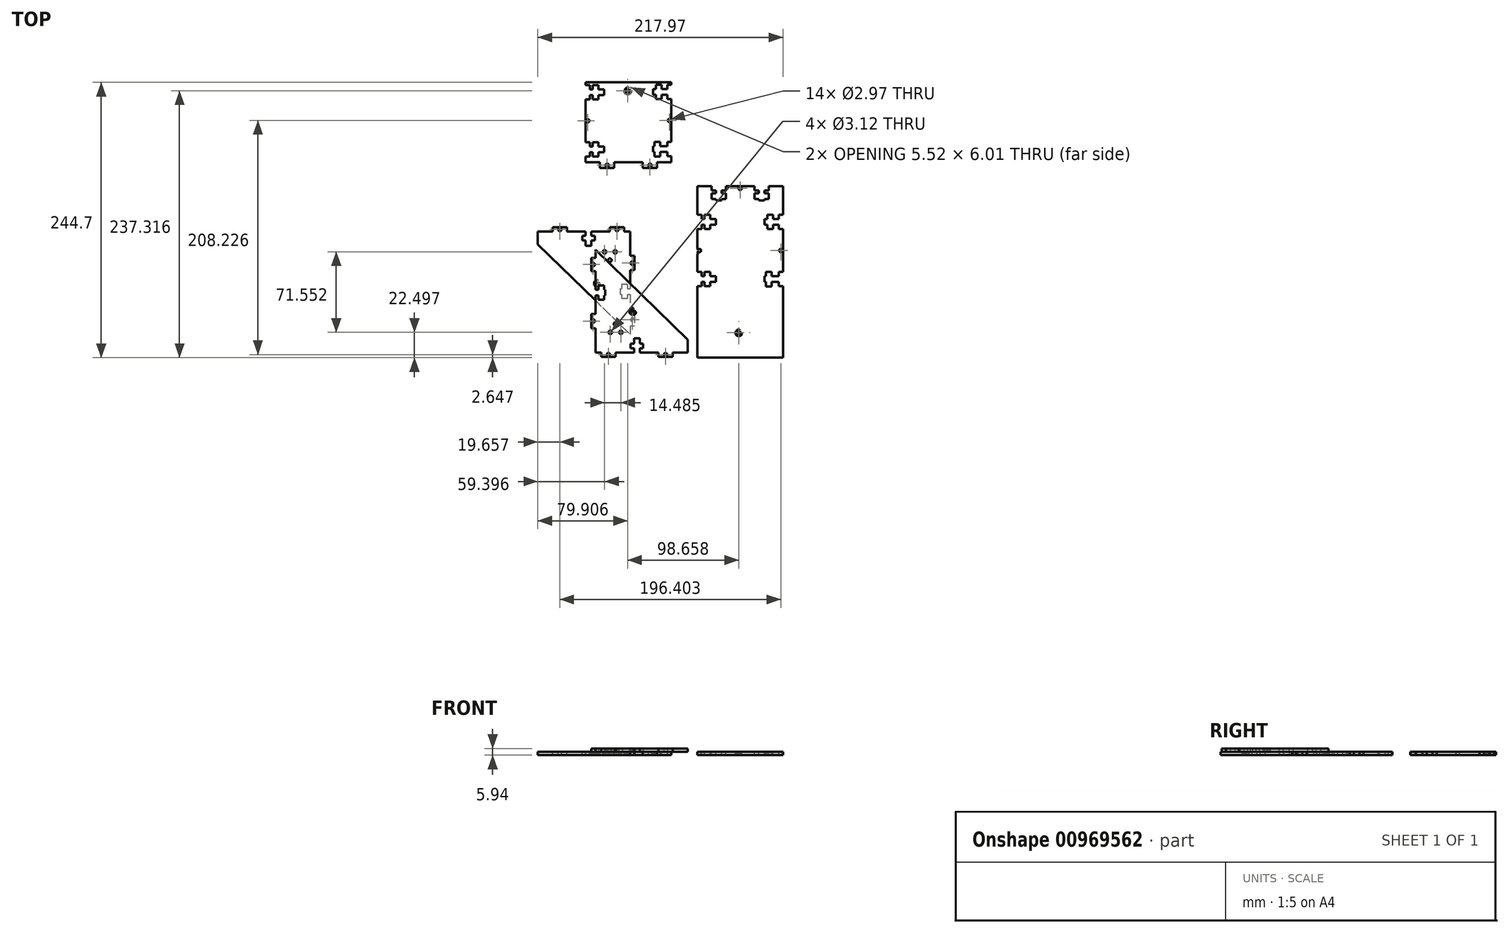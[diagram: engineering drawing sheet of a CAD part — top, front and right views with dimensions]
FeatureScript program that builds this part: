
annotation { "Feature Type Name" : "Feature", "Feature Type Description" : "" }
export const myFeature = defineFeature(function(context is Context, id is Id, definition is map)
    precondition{}
    {
        {
            var Q0;
            Q0=qCreatedBy(makeId("Top.planeOp"),FACE);
            var sketch = newSketch(context, id + "F0", { "sketchPlane" : qUnion([Q0])});
            skLineSegment(sketch, "E0.bottom", {"start": v(-31.04, 87.19) * mm, "end": v(45.16, 87.19) * mm});
            skLineSegment(sketch, "E0.top", {"start": v(-31.04, -65.21) * mm, "end": v(45.16, -65.21) * mm});
            skLineSegment(sketch, "E0.left", {"start": v(-31.04, 87.19) * mm, "end": v(-31.04, -65.21) * mm});
            skLineSegment(sketch, "E0.right", {"start": v(45.16, 87.19) * mm, "end": v(45.16, -65.21) * mm});
            skSolve(sketch);
        }
        {
            var Q0;
            Q0 = qSketchRegion(id + "F0", true);
            extrude(context, id + "F1", {"entities" : qUnion([Q0]), "depth" : 2.97 * mm, "offsetDistance" : 25.4 * mm});
        }
        {
            var Q0;
            Q0=makeQuery(id+"F1.opExtrude","CAP_FACE",FACE,{"disambiguationData":[OSD([sQuery(id+"F0.wireOp",EDGE,"E0.bottom"),sQuery(id+"F0.wireOp",EDGE,"E0.top"),sQuery(id+"F0.wireOp",EDGE,"E0.left"),sQuery(id+"F0.wireOp",EDGE,"E0.right")])],"isStart":false});
            var sketch = newSketch(context, id + "F2", { "sketchPlane" : qUnion([Q0])});
            skLineSegment(sketch, "E1.bottom", {"start": v(-31.04, 61.79) * mm, "end": v(-27.23, 61.79) * mm});
            skLineSegment(sketch, "E1.top", {"start": v(-31.04, 49.09) * mm, "end": v(-27.23, 49.09) * mm});
            skLineSegment(sketch, "E1.left", {"start": v(-31.04, 61.79) * mm, "end": v(-31.04, 49.09) * mm});
            skLineSegment(sketch, "E1.right", {"start": v(-27.23, 61.79) * mm, "end": v(-27.23, 49.09) * mm});
            skLineSegment(sketch, "E2", {"start": v(-24.7, 61.79) * mm, "end": v(-24.7, 87.19) * mm, "construction": true});
            skLineSegment(sketch, "E3", {"start": v(-31.04, 33.1) * mm, "end": v(-31.04, 33.1) * mm});
            skLineSegment(sketch, "E4.bottom", {"start": v(-14.53, 52.9) * mm, "end": v(-39.93, 52.9) * mm});
            skLineSegment(sketch, "E4.top", {"start": v(-14.53, 57.98) * mm, "end": v(-39.93, 57.98) * mm});
            skLineSegment(sketch, "E4.left", {"start": v(-14.53, 52.9) * mm, "end": v(-14.53, 57.98) * mm});
            skLineSegment(sketch, "E4.right", {"start": v(-39.93, 52.9) * mm, "end": v(-39.93, 57.98) * mm});
            skPoint(sketch, "E4.middle", {"position": v(-27.23, 55.44) * mm});
            skLineSegment(sketch, "E5.bottom", {"start": v(-24.7, 61.79) * mm, "end": v(-19.61, 61.79) * mm});
            skLineSegment(sketch, "E5.top", {"start": v(-24.7, 49.09) * mm, "end": v(-19.61, 49.09) * mm});
            skLineSegment(sketch, "E5.left", {"start": v(-24.7, 61.79) * mm, "end": v(-24.7, 49.09) * mm});
            skLineSegment(sketch, "E5.right", {"start": v(-19.61, 61.79) * mm, "end": v(-19.61, 49.09) * mm});
            skLineSegment(sketch, "E6.bottom", {"start": v(-31.04, 10.99) * mm, "end": v(-27.23, 10.99) * mm});
            skLineSegment(sketch, "E6.top", {"start": v(-31.04, -1.71) * mm, "end": v(-27.23, -1.71) * mm});
            skLineSegment(sketch, "E6.left", {"start": v(-31.04, 10.99) * mm, "end": v(-31.04, -1.71) * mm});
            skLineSegment(sketch, "E6.right", {"start": v(-27.23, 10.99) * mm, "end": v(-27.23, -1.71) * mm});
            skLineSegment(sketch, "E7", {"start": v(11.23, 8.06) * mm, "end": v(11.23, 8.06) * mm});
            skLineSegment(sketch, "E8.bottom", {"start": v(-14.53, 2.1) * mm, "end": v(-39.93, 2.1) * mm});
            skLineSegment(sketch, "E8.top", {"start": v(-14.53, 7.18) * mm, "end": v(-39.93, 7.18) * mm});
            skLineSegment(sketch, "E8.left", {"start": v(-14.53, 2.1) * mm, "end": v(-14.53, 7.18) * mm});
            skLineSegment(sketch, "E8.right", {"start": v(-39.93, 2.1) * mm, "end": v(-39.93, 7.18) * mm});
            skPoint(sketch, "E8.middle", {"position": v(-27.23, 4.64) * mm});
            skLineSegment(sketch, "E9.bottom", {"start": v(-24.7, 10.99) * mm, "end": v(-19.61, 10.99) * mm});
            skLineSegment(sketch, "E9.top", {"start": v(-24.7, -1.71) * mm, "end": v(-19.61, -1.71) * mm});
            skLineSegment(sketch, "E9.left", {"start": v(-24.7, 10.99) * mm, "end": v(-24.7, -1.71) * mm});
            skLineSegment(sketch, "E9.right", {"start": v(-19.61, 10.99) * mm, "end": v(-19.61, -1.71) * mm});
            skLineSegment(sketch, "E10.bottom", {"start": v(-18.34, 87.19) * mm, "end": v(-5.64, 87.19) * mm});
            skLineSegment(sketch, "E10.top", {"start": v(-18.34, 83.38) * mm, "end": v(-5.64, 83.38) * mm});
            skLineSegment(sketch, "E10.left", {"start": v(-18.34, 87.19) * mm, "end": v(-18.34, 83.38) * mm});
            skLineSegment(sketch, "E10.right", {"start": v(-5.64, 87.19) * mm, "end": v(-5.64, 83.38) * mm});
            skLineSegment(sketch, "E11.bottom", {"start": v(19.76, 87.19) * mm, "end": v(32.46, 87.19) * mm});
            skLineSegment(sketch, "E11.top", {"start": v(19.76, 83.38) * mm, "end": v(32.46, 83.38) * mm});
            skLineSegment(sketch, "E11.left", {"start": v(19.76, 87.19) * mm, "end": v(19.76, 83.38) * mm});
            skLineSegment(sketch, "E11.right", {"start": v(32.46, 87.19) * mm, "end": v(32.46, 83.38) * mm});
            skLineSegment(sketch, "E12", {"start": v(-18.34, 85.28) * mm, "end": v(-31.04, 85.28) * mm, "construction": true});
            skLineSegment(sketch, "E13", {"start": v(32.46, 85.28) * mm, "end": v(45.16, 85.28) * mm, "construction": true});
            skLineSegment(sketch, "E14.bottom", {"start": v(-9.45, 74.49) * mm, "end": v(-14.53, 74.49) * mm});
            skLineSegment(sketch, "E14.top", {"start": v(-9.45, 99.89) * mm, "end": v(-14.53, 99.89) * mm});
            skLineSegment(sketch, "E14.left", {"start": v(-9.45, 74.49) * mm, "end": v(-9.45, 99.89) * mm});
            skLineSegment(sketch, "E14.right", {"start": v(-14.53, 74.49) * mm, "end": v(-14.53, 99.89) * mm});
            skPoint(sketch, "E14.middle", {"position": v(-12, 87.19) * mm});
            skLineSegment(sketch, "E15.bottom", {"start": v(-5.64, 80.84) * mm, "end": v(-18.34, 80.84) * mm});
            skLineSegment(sketch, "E15.top", {"start": v(-5.64, 75.76) * mm, "end": v(-18.34, 75.76) * mm});
            skLineSegment(sketch, "E15.left", {"start": v(-5.64, 80.84) * mm, "end": v(-5.64, 75.76) * mm});
            skLineSegment(sketch, "E15.right", {"start": v(-18.34, 80.84) * mm, "end": v(-18.34, 75.76) * mm});
            skLineSegment(sketch, "E16", {"start": v(-5.64, 80.84) * mm, "end": v(-5.64, 83.38) * mm, "construction": true});
            skLineSegment(sketch, "E17.bottom", {"start": v(28.65, 74.49) * mm, "end": v(23.57, 74.49) * mm});
            skLineSegment(sketch, "E17.top", {"start": v(28.65, 99.89) * mm, "end": v(23.57, 99.89) * mm});
            skLineSegment(sketch, "E17.left", {"start": v(28.65, 74.49) * mm, "end": v(28.65, 99.89) * mm});
            skLineSegment(sketch, "E17.right", {"start": v(23.57, 74.49) * mm, "end": v(23.57, 99.89) * mm});
            skPoint(sketch, "E17.middle", {"position": v(26.1, 87.19) * mm});
            skLineSegment(sketch, "E18.bottom", {"start": v(32.46, 80.84) * mm, "end": v(19.76, 80.84) * mm});
            skLineSegment(sketch, "E18.top", {"start": v(32.46, 75.76) * mm, "end": v(19.76, 75.76) * mm});
            skLineSegment(sketch, "E18.left", {"start": v(32.46, 80.84) * mm, "end": v(32.46, 75.76) * mm});
            skLineSegment(sketch, "E18.right", {"start": v(19.76, 80.84) * mm, "end": v(19.76, 75.76) * mm});
            skLineSegment(sketch, "E19", {"start": v(19.76, 80.84) * mm, "end": v(19.76, 83.38) * mm, "construction": true});
            skLineSegment(sketch, "E20", {"start": v(-29.14, 49.09) * mm, "end": v(-29.14, 10.99) * mm, "construction": true});
            skCircle(sketch, "E21", {"center": v(-29.14, 30.04) * mm, "radius": 1.49 * mm});
            skLineSegment(sketch, "E22", {"start": v(-5.64, 85.28) * mm, "end": v(19.76, 85.28) * mm, "construction": true});
            skCircle(sketch, "E23", {"center": v(7.06, 85.28) * mm, "radius": 1.49 * mm});
            skLineSegment(sketch, "E24", {"start": v(-27.23, 49.09) * mm, "end": v(-24.7, 49.09) * mm, "construction": true});
            skLineSegment(sketch, "E25.bottom", {"start": v(45.16, 61.79) * mm, "end": v(41.35, 61.79) * mm});
            skLineSegment(sketch, "E25.top", {"start": v(45.16, 49.09) * mm, "end": v(41.35, 49.09) * mm});
            skLineSegment(sketch, "E25.left", {"start": v(45.16, 61.79) * mm, "end": v(45.16, 49.09) * mm});
            skLineSegment(sketch, "E25.right", {"start": v(41.35, 61.79) * mm, "end": v(41.35, 49.09) * mm});
            skLineSegment(sketch, "E26", {"start": v(41.35, 61.79) * mm, "end": v(41.35, 87.19) * mm, "construction": true});
            skLineSegment(sketch, "E27.bottom", {"start": v(28.65, 57.98) * mm, "end": v(54.05, 57.98) * mm});
            skLineSegment(sketch, "E27.top", {"start": v(28.65, 52.9) * mm, "end": v(54.05, 52.9) * mm});
            skLineSegment(sketch, "E27.left", {"start": v(28.65, 57.98) * mm, "end": v(28.65, 52.9) * mm});
            skLineSegment(sketch, "E27.right", {"start": v(54.05, 57.98) * mm, "end": v(54.05, 52.9) * mm});
            skPoint(sketch, "E27.middle", {"position": v(41.35, 55.44) * mm});
            skLineSegment(sketch, "E28.bottom", {"start": v(36.27, 61.79) * mm, "end": v(31.19, 61.79) * mm});
            skLineSegment(sketch, "E28.top", {"start": v(36.27, 49.09) * mm, "end": v(31.19, 49.09) * mm});
            skLineSegment(sketch, "E28.left", {"start": v(36.27, 61.79) * mm, "end": v(36.27, 49.09) * mm});
            skLineSegment(sketch, "E28.right", {"start": v(31.19, 61.79) * mm, "end": v(31.19, 49.09) * mm});
            skLineSegment(sketch, "E29", {"start": v(36.27, 49.09) * mm, "end": v(41.35, 49.09) * mm, "construction": true});
            skLineSegment(sketch, "E30.bottom", {"start": v(45.16, 10.99) * mm, "end": v(41.35, 10.99) * mm});
            skLineSegment(sketch, "E30.top", {"start": v(45.16, -1.71) * mm, "end": v(41.35, -1.71) * mm});
            skLineSegment(sketch, "E30.left", {"start": v(45.16, 10.99) * mm, "end": v(45.16, -1.71) * mm});
            skLineSegment(sketch, "E30.right", {"start": v(41.35, 10.99) * mm, "end": v(41.35, -1.71) * mm});
            skLineSegment(sketch, "E31.bottom", {"start": v(28.65, 7.18) * mm, "end": v(54.05, 7.18) * mm});
            skLineSegment(sketch, "E31.top", {"start": v(28.65, 2.1) * mm, "end": v(54.05, 2.1) * mm});
            skLineSegment(sketch, "E31.left", {"start": v(28.65, 7.18) * mm, "end": v(28.65, 2.1) * mm});
            skLineSegment(sketch, "E31.right", {"start": v(54.05, 7.18) * mm, "end": v(54.05, 2.1) * mm});
            skPoint(sketch, "E31.middle", {"position": v(41.35, 4.64) * mm});
            skLineSegment(sketch, "E32.bottom", {"start": v(34.98, 10.99) * mm, "end": v(30.02, 10.99) * mm});
            skLineSegment(sketch, "E32.top", {"start": v(34.98, -2) * mm, "end": v(30.02, -2) * mm});
            skLineSegment(sketch, "E32.left", {"start": v(34.98, 10.99) * mm, "end": v(34.98, -2) * mm});
            skLineSegment(sketch, "E32.right", {"start": v(30.02, 10.99) * mm, "end": v(30.02, -2) * mm});
            skLineSegment(sketch, "E33", {"start": v(41.35, 49.09) * mm, "end": v(43.25, 49.09) * mm, "construction": true});
            skLineSegment(sketch, "E34", {"start": v(43.25, 10.99) * mm, "end": v(43.25, 49.09) * mm, "construction": true});
            skCircle(sketch, "E35", {"center": v(43.25, 30.04) * mm, "radius": 1.49 * mm});
            skSolve(sketch);
        }
        {
            var Q0;
            Q0 = qSketchRegion(id + "F2", true);
            extrude(context, id + "F3", {"entities" : qUnion([Q0]), "operationType" : NewBodyOperationType.REMOVE, "oppositeDirection" : true, "depth" : 25.4 * mm, "offsetDistance" : 25.4 * mm});
        }
        {
            var Q0;
            Q0=qCreatedBy(makeId("Top.planeOp"),FACE);
            var sketch = newSketch(context, id + "F4", { "sketchPlane" : qUnion([Q0])});
            skLineSegment(sketch, "E36.bottom", {"start": v(-43.25, 86.15) * mm, "end": v(-129.12, 86.15) * mm});
            skLineSegment(sketch, "E36.top", {"start": v(-43.25, -66.25) * mm, "end": v(-129.12, -66.25) * mm});
            skLineSegment(sketch, "E36.left", {"start": v(-43.25, 86.15) * mm, "end": v(-43.25, -66.25) * mm});
            skLineSegment(sketch, "E36.right", {"start": v(-129.12, 86.15) * mm, "end": v(-129.12, -66.25) * mm});
            skSolve(sketch);
        }
        {
            var Q0;
            Q0 = qSketchRegion(id + "F4", true);
            extrude(context, id + "F5", {"entities" : qUnion([Q0]), "depth" : 2.97 * mm, "offsetDistance" : 25.4 * mm});
        }
        {
            var Q0;
            Q0=makeQuery(id+"F5.opExtrude","CAP_FACE",FACE,{"disambiguationData":[OSD([sQuery(id+"F4.wireOp",EDGE,"E36.bottom"),sQuery(id+"F4.wireOp",EDGE,"E36.top"),sQuery(id+"F4.wireOp",EDGE,"E36.left"),sQuery(id+"F4.wireOp",EDGE,"E36.right")])],"isStart":false});
            var sketch = newSketch(context, id + "F6", { "sketchPlane" : qUnion([Q0])});
            skLineSegment(sketch, "E37.bottom", {"start": v(-43.25, 86.15) * mm, "end": v(-47.06, 86.15) * mm});
            skLineSegment(sketch, "E37.top", {"start": v(-43.25, 60.75) * mm, "end": v(-47.06, 60.75) * mm});
            skLineSegment(sketch, "E37.left", {"start": v(-43.25, 86.15) * mm, "end": v(-43.25, 60.75) * mm});
            skLineSegment(sketch, "E37.right", {"start": v(-47.06, 86.15) * mm, "end": v(-47.06, 60.75) * mm});
            skLineSegment(sketch, "E38", {"start": v(-46.12, 86.15) * mm, "end": v(-46.12, 86.15) * mm});
            skLineSegment(sketch, "E39", {"start": v(-43.25, 68.93) * mm, "end": v(-43.25, 68.93) * mm});
            skLineSegment(sketch, "E40.bottom", {"start": v(-43.25, 48.05) * mm, "end": v(-47.06, 48.05) * mm});
            skLineSegment(sketch, "E40.top", {"start": v(-43.25, 9.95) * mm, "end": v(-47.06, 9.95) * mm});
            skLineSegment(sketch, "E40.left", {"start": v(-43.25, 48.05) * mm, "end": v(-43.25, 9.95) * mm});
            skLineSegment(sketch, "E40.right", {"start": v(-47.06, 48.05) * mm, "end": v(-47.06, 9.95) * mm});
            skLineSegment(sketch, "E41", {"start": v(-45.15, 60.75) * mm, "end": v(-45.15, 48.05) * mm, "construction": true});
            skLineSegment(sketch, "E42.bottom", {"start": v(-43.25, -1.8) * mm, "end": v(-47.06, -1.8) * mm});
            skLineSegment(sketch, "E42.top", {"start": v(-43.25, -174.53) * mm, "end": v(-47.06, -174.53) * mm});
            skLineSegment(sketch, "E42.left", {"start": v(-43.25, -1.8) * mm, "end": v(-43.25, -174.53) * mm});
            skLineSegment(sketch, "E42.right", {"start": v(-47.06, -1.8) * mm, "end": v(-47.06, -174.53) * mm});
            skLineSegment(sketch, "E43.bottom", {"start": v(-43.25, 35.35) * mm, "end": v(-47.06, 35.35) * mm});
            skLineSegment(sketch, "E43.top", {"start": v(-43.25, 22.65) * mm, "end": v(-47.06, 22.65) * mm});
            skLineSegment(sketch, "E43.left", {"start": v(-43.25, 35.35) * mm, "end": v(-43.25, 22.65) * mm});
            skLineSegment(sketch, "E43.right", {"start": v(-47.06, 35.35) * mm, "end": v(-47.06, 22.65) * mm});
            skLineSegment(sketch, "E44", {"start": v(-45.15, 48.05) * mm, "end": v(-45.15, 35.35) * mm, "construction": true});
            skLineSegment(sketch, "E45", {"start": v(-45.15, 9.95) * mm, "end": v(-45.15, 22.65) * mm, "construction": true});
            skLineSegment(sketch, "E46.bottom", {"start": v(-55.95, 31.54) * mm, "end": v(-30.55, 31.54) * mm});
            skLineSegment(sketch, "E46.top", {"start": v(-55.95, 26.46) * mm, "end": v(-30.55, 26.46) * mm});
            skLineSegment(sketch, "E46.left", {"start": v(-55.95, 31.54) * mm, "end": v(-55.95, 26.46) * mm});
            skLineSegment(sketch, "E46.right", {"start": v(-30.55, 31.54) * mm, "end": v(-30.55, 26.46) * mm});
            skPoint(sketch, "E46.middle", {"position": v(-43.25, 29) * mm});
            skLineSegment(sketch, "E47.bottom", {"start": v(-49.6, 35.35) * mm, "end": v(-54.68, 35.35) * mm});
            skLineSegment(sketch, "E47.top", {"start": v(-49.6, 22.65) * mm, "end": v(-54.68, 22.65) * mm});
            skLineSegment(sketch, "E47.left", {"start": v(-49.6, 35.35) * mm, "end": v(-49.6, 22.65) * mm});
            skLineSegment(sketch, "E47.right", {"start": v(-54.68, 35.35) * mm, "end": v(-54.68, 22.65) * mm});
            skLineSegment(sketch, "E48", {"start": v(-49.6, 33.67) * mm, "end": v(-47.06, 33.67) * mm, "construction": true});
            skCircle(sketch, "E49", {"center": v(-45.15, 54.4) * mm, "radius": 1.49 * mm});
            skLineSegment(sketch, "E50", {"start": v(-45.15, 9.95) * mm, "end": v(-45.15, -1.8) * mm, "construction": true});
            skCircle(sketch, "E51", {"center": v(-45.15, 4.08) * mm, "radius": 1.49 * mm});
            skLineSegment(sketch, "E52.bottom", {"start": v(-47.06, 82.34) * mm, "end": v(-52.31, 82.34) * mm});
            skLineSegment(sketch, "E52.top", {"start": v(-47.06, 86.15) * mm, "end": v(-52.31, 86.15) * mm});
            skLineSegment(sketch, "E52.left", {"start": v(-47.06, 82.34) * mm, "end": v(-47.06, 86.15) * mm});
            skLineSegment(sketch, "E52.right", {"start": v(-52.31, 82.34) * mm, "end": v(-52.31, 86.15) * mm});
            skLineSegment(sketch, "E53", {"start": v(-52.31, 82.34) * mm, "end": v(-65.01, 82.34) * mm, "construction": true});
            skLineSegment(sketch, "E54.bottom", {"start": v(-65.01, 82.34) * mm, "end": v(-103.11, 82.34) * mm});
            skLineSegment(sketch, "E54.top", {"start": v(-65.01, 86.15) * mm, "end": v(-103.11, 86.15) * mm});
            skLineSegment(sketch, "E54.left", {"start": v(-65.01, 82.34) * mm, "end": v(-65.01, 86.15) * mm});
            skLineSegment(sketch, "E54.right", {"start": v(-103.11, 82.34) * mm, "end": v(-103.11, 86.15) * mm});
            skLineSegment(sketch, "E55", {"start": v(-103.11, 82.34) * mm, "end": v(-115.81, 82.34) * mm, "construction": true});
            skLineSegment(sketch, "E56.bottom", {"start": v(-115.81, 82.34) * mm, "end": v(-130.63, 82.34) * mm});
            skLineSegment(sketch, "E56.top", {"start": v(-115.81, 87.7) * mm, "end": v(-130.63, 87.7) * mm});
            skLineSegment(sketch, "E56.left", {"start": v(-115.81, 82.34) * mm, "end": v(-115.81, 87.7) * mm});
            skLineSegment(sketch, "E56.right", {"start": v(-130.63, 82.34) * mm, "end": v(-130.63, 87.7) * mm});
            skLineSegment(sketch, "E57", {"start": v(-103.11, 84.25) * mm, "end": v(-115.81, 84.25) * mm, "construction": true});
            skCircle(sketch, "E58", {"center": v(-109.46, 84.25) * mm, "radius": 1.49 * mm});
            skLineSegment(sketch, "E59", {"start": v(-65.01, 84.25) * mm, "end": v(-52.31, 84.25) * mm, "construction": true});
            skCircle(sketch, "E60", {"center": v(-58.66, 84.25) * mm, "radius": 1.49 * mm});
            skLineSegment(sketch, "E61.bottom", {"start": v(-86.6, 69.64) * mm, "end": v(-81.52, 69.64) * mm});
            skLineSegment(sketch, "E61.top", {"start": v(-86.6, 95.04) * mm, "end": v(-81.52, 95.04) * mm});
            skLineSegment(sketch, "E61.left", {"start": v(-86.6, 69.64) * mm, "end": v(-86.6, 95.04) * mm});
            skLineSegment(sketch, "E61.right", {"start": v(-81.52, 69.64) * mm, "end": v(-81.52, 95.04) * mm});
            skPoint(sketch, "E61.middle", {"position": v(-84.06, 82.34) * mm});
            skLineSegment(sketch, "E62.bottom", {"start": v(-89.43, 78.63) * mm, "end": v(-78.4, 78.63) * mm});
            skLineSegment(sketch, "E62.top", {"start": v(-89.43, 74.47) * mm, "end": v(-78.4, 74.47) * mm});
            skLineSegment(sketch, "E62.left", {"start": v(-89.43, 78.63) * mm, "end": v(-89.43, 74.47) * mm});
            skLineSegment(sketch, "E62.right", {"start": v(-78.4, 78.63) * mm, "end": v(-78.4, 74.47) * mm});
            skSolve(sketch);
        }
        {
            var Q0;
            Q0 = qSketchRegion(id + "F6", true);
            extrude(context, id + "F7", {"entities" : qUnion([Q0]), "operationType" : NewBodyOperationType.REMOVE, "oppositeDirection" : true, "depth" : 25.4 * mm, "offsetDistance" : 25.4 * mm});
        }
        {
            var Q0;
            Q0=qCreatedBy(makeId("Top.planeOp"),FACE);
            var sketch = newSketch(context, id + "F8", { "sketchPlane" : qUnion([Q0])});
            skLineSegment(sketch, "E63.bottom", {"start": v(-30.12, 88.56) * mm, "end": v(46.08, 88.56) * mm});
            skLineSegment(sketch, "E63.top", {"start": v(-30.12, 164.76) * mm, "end": v(46.08, 164.76) * mm});
            skLineSegment(sketch, "E63.left", {"start": v(-30.12, 88.56) * mm, "end": v(-30.12, 164.76) * mm});
            skLineSegment(sketch, "E63.right", {"start": v(46.08, 88.56) * mm, "end": v(46.08, 164.76) * mm});
            skSolve(sketch);
        }
        {
            var Q0;
            Q0 = qSketchRegion(id + "F8", true);
            extrude(context, id + "F9", {"entities" : qUnion([Q0]), "depth" : 2.97 * mm, "offsetDistance" : 25.4 * mm});
        }
        {
            var Q0;
            Q0=makeQuery(id+"F9.opExtrude","CAP_FACE",FACE,{"disambiguationData":[OSD([sQuery(id+"F8.wireOp",EDGE,"E63.bottom"),sQuery(id+"F8.wireOp",EDGE,"E63.top"),sQuery(id+"F8.wireOp",EDGE,"E63.left"),sQuery(id+"F8.wireOp",EDGE,"E63.right")])],"isStart":false});
            var sketch = newSketch(context, id + "F10", { "sketchPlane" : qUnion([Q0])});
            skLineSegment(sketch, "E64.bottom", {"start": v(-30.12, 93.64) * mm, "end": v(-17.42, 93.64) * mm});
            skLineSegment(sketch, "E64.top", {"start": v(-30.12, 88.56) * mm, "end": v(-17.42, 88.56) * mm});
            skLineSegment(sketch, "E64.left", {"start": v(-30.12, 93.64) * mm, "end": v(-30.12, 88.56) * mm});
            skLineSegment(sketch, "E64.right", {"start": v(-17.42, 93.64) * mm, "end": v(-17.42, 88.56) * mm});
            skLineSegment(sketch, "E65.bottom", {"start": v(-4.72, 93.64) * mm, "end": v(20.68, 93.64) * mm});
            skLineSegment(sketch, "E65.top", {"start": v(-4.72, 88.56) * mm, "end": v(20.68, 88.56) * mm});
            skLineSegment(sketch, "E65.left", {"start": v(-4.72, 93.64) * mm, "end": v(-4.72, 88.56) * mm});
            skLineSegment(sketch, "E65.right", {"start": v(20.68, 93.64) * mm, "end": v(20.68, 88.56) * mm});
            skLineSegment(sketch, "E66", {"start": v(-17.42, 91.1) * mm, "end": v(-4.72, 91.1) * mm, "construction": true});
            skCircle(sketch, "E67", {"center": v(-11.07, 91.1) * mm, "radius": 1.49 * mm});
            skLineSegment(sketch, "E68.bottom", {"start": v(46.08, 88.56) * mm, "end": v(33.38, 88.56) * mm});
            skLineSegment(sketch, "E68.top", {"start": v(46.08, 93.65) * mm, "end": v(33.38, 93.65) * mm});
            skLineSegment(sketch, "E68.left", {"start": v(46.08, 88.56) * mm, "end": v(46.08, 93.65) * mm});
            skLineSegment(sketch, "E68.right", {"start": v(33.38, 88.56) * mm, "end": v(33.38, 93.65) * mm});
            skLineSegment(sketch, "E69", {"start": v(20.68, 91.1) * mm, "end": v(33.38, 91.1) * mm, "construction": true});
            skCircle(sketch, "E70", {"center": v(27.03, 91.1) * mm, "radius": 1.49 * mm});
            skLineSegment(sketch, "E71.bottom", {"start": v(-30.23, 162.4) * mm, "end": v(-26.42, 162.4) * mm});
            skLineSegment(sketch, "E71.top", {"start": v(-30.23, 149.7) * mm, "end": v(-26.42, 149.7) * mm});
            skLineSegment(sketch, "E71.left", {"start": v(-30.23, 162.4) * mm, "end": v(-30.23, 149.7) * mm});
            skLineSegment(sketch, "E71.right", {"start": v(-26.42, 162.4) * mm, "end": v(-26.42, 149.7) * mm});
            skLineSegment(sketch, "E72", {"start": v(-23.88, 162.4) * mm, "end": v(-23.88, 187.8) * mm, "construction": true});
            skLineSegment(sketch, "E73", {"start": v(27.43, 133.71) * mm, "end": v(27.43, 133.71) * mm});
            skLineSegment(sketch, "E74.bottom", {"start": v(-13.72, 153.5) * mm, "end": v(-39.12, 153.5) * mm});
            skLineSegment(sketch, "E74.top", {"start": v(-13.72, 158.59) * mm, "end": v(-39.12, 158.59) * mm});
            skLineSegment(sketch, "E74.left", {"start": v(-13.72, 153.5) * mm, "end": v(-13.72, 158.59) * mm});
            skLineSegment(sketch, "E74.right", {"start": v(-39.12, 153.5) * mm, "end": v(-39.12, 158.59) * mm});
            skPoint(sketch, "E74.middle", {"position": v(-26.42, 156.05) * mm});
            skLineSegment(sketch, "E75.bottom", {"start": v(-23.88, 162.4) * mm, "end": v(-18.8, 162.4) * mm});
            skLineSegment(sketch, "E75.top", {"start": v(-23.88, 149.7) * mm, "end": v(-18.8, 149.7) * mm});
            skLineSegment(sketch, "E75.left", {"start": v(-23.88, 162.4) * mm, "end": v(-23.88, 149.7) * mm});
            skLineSegment(sketch, "E75.right", {"start": v(-18.8, 162.4) * mm, "end": v(-18.8, 149.7) * mm});
            skLineSegment(sketch, "E76.bottom", {"start": v(-30.23, 111.6) * mm, "end": v(-26.42, 111.6) * mm});
            skLineSegment(sketch, "E76.top", {"start": v(-30.23, 98.9) * mm, "end": v(-26.42, 98.9) * mm});
            skLineSegment(sketch, "E76.left", {"start": v(-30.23, 111.6) * mm, "end": v(-30.23, 98.9) * mm});
            skLineSegment(sketch, "E76.right", {"start": v(-26.42, 111.6) * mm, "end": v(-26.42, 98.9) * mm});
            skLineSegment(sketch, "E77.bottom", {"start": v(-13.72, 102.7) * mm, "end": v(-39.12, 102.7) * mm});
            skLineSegment(sketch, "E77.top", {"start": v(-13.72, 107.79) * mm, "end": v(-39.12, 107.79) * mm});
            skLineSegment(sketch, "E77.left", {"start": v(-13.72, 102.7) * mm, "end": v(-13.72, 107.79) * mm});
            skLineSegment(sketch, "E77.right", {"start": v(-39.12, 102.7) * mm, "end": v(-39.12, 107.79) * mm});
            skPoint(sketch, "E77.middle", {"position": v(-26.42, 105.25) * mm});
            skLineSegment(sketch, "E78.bottom", {"start": v(-23.88, 111.6) * mm, "end": v(-18.8, 111.6) * mm});
            skLineSegment(sketch, "E78.top", {"start": v(-23.88, 98.9) * mm, "end": v(-18.8, 98.9) * mm});
            skLineSegment(sketch, "E78.left", {"start": v(-23.88, 111.6) * mm, "end": v(-23.88, 98.9) * mm});
            skLineSegment(sketch, "E78.right", {"start": v(-18.8, 111.6) * mm, "end": v(-18.8, 98.9) * mm});
            skLineSegment(sketch, "E79", {"start": v(-28.32, 149.7) * mm, "end": v(-28.32, 111.6) * mm, "construction": true});
            skCircle(sketch, "E80", {"center": v(-28.32, 130.65) * mm, "radius": 1.49 * mm});
            skLineSegment(sketch, "E81", {"start": v(-26.42, 149.7) * mm, "end": v(-23.88, 149.7) * mm, "construction": true});
            skLineSegment(sketch, "E82.bottom", {"start": v(46.27, 162.68) * mm, "end": v(42.46, 162.68) * mm});
            skLineSegment(sketch, "E82.top", {"start": v(46.27, 149.98) * mm, "end": v(42.46, 149.98) * mm});
            skLineSegment(sketch, "E82.left", {"start": v(46.27, 162.68) * mm, "end": v(46.27, 149.98) * mm});
            skLineSegment(sketch, "E82.right", {"start": v(42.46, 162.68) * mm, "end": v(42.46, 149.98) * mm});
            skLineSegment(sketch, "E83.bottom", {"start": v(29.76, 158.87) * mm, "end": v(55.16, 158.87) * mm});
            skLineSegment(sketch, "E83.top", {"start": v(29.76, 153.8) * mm, "end": v(55.16, 153.8) * mm});
            skLineSegment(sketch, "E83.left", {"start": v(29.76, 158.87) * mm, "end": v(29.76, 153.8) * mm});
            skLineSegment(sketch, "E83.right", {"start": v(55.16, 158.87) * mm, "end": v(55.16, 153.8) * mm});
            skPoint(sketch, "E83.middle", {"position": v(42.46, 156.33) * mm});
            skLineSegment(sketch, "E84.bottom", {"start": v(37.38, 162.68) * mm, "end": v(32.3, 162.68) * mm});
            skLineSegment(sketch, "E84.top", {"start": v(37.38, 149.98) * mm, "end": v(32.3, 149.98) * mm});
            skLineSegment(sketch, "E84.left", {"start": v(37.38, 162.68) * mm, "end": v(37.38, 149.98) * mm});
            skLineSegment(sketch, "E84.right", {"start": v(32.3, 162.68) * mm, "end": v(32.3, 149.98) * mm});
            skLineSegment(sketch, "E85", {"start": v(37.38, 149.98) * mm, "end": v(42.46, 149.98) * mm, "construction": true});
            skLineSegment(sketch, "E86.bottom", {"start": v(46.27, 111.88) * mm, "end": v(42.46, 111.88) * mm});
            skLineSegment(sketch, "E86.top", {"start": v(46.27, 99.18) * mm, "end": v(42.46, 99.18) * mm});
            skLineSegment(sketch, "E86.left", {"start": v(46.27, 111.88) * mm, "end": v(46.27, 99.18) * mm});
            skLineSegment(sketch, "E86.right", {"start": v(42.46, 111.88) * mm, "end": v(42.46, 99.18) * mm});
            skLineSegment(sketch, "E87.bottom", {"start": v(29.76, 108.07) * mm, "end": v(55.16, 108.07) * mm});
            skLineSegment(sketch, "E87.top", {"start": v(29.76, 103) * mm, "end": v(55.16, 103) * mm});
            skLineSegment(sketch, "E87.left", {"start": v(29.76, 108.07) * mm, "end": v(29.76, 103) * mm});
            skLineSegment(sketch, "E87.right", {"start": v(55.16, 108.07) * mm, "end": v(55.16, 103) * mm});
            skPoint(sketch, "E87.middle", {"position": v(42.46, 105.53) * mm});
            skLineSegment(sketch, "E88.bottom", {"start": v(36.1, 111.88) * mm, "end": v(31.14, 111.88) * mm});
            skLineSegment(sketch, "E88.top", {"start": v(36.1, 98.9) * mm, "end": v(31.14, 98.9) * mm});
            skLineSegment(sketch, "E88.left", {"start": v(36.1, 111.88) * mm, "end": v(36.1, 98.9) * mm});
            skLineSegment(sketch, "E88.right", {"start": v(31.14, 111.88) * mm, "end": v(31.14, 98.9) * mm});
            skLineSegment(sketch, "E89", {"start": v(42.46, 149.98) * mm, "end": v(44.37, 149.98) * mm, "construction": true});
            skLineSegment(sketch, "E90", {"start": v(44.37, 111.88) * mm, "end": v(44.37, 149.98) * mm, "construction": true});
            skCircle(sketch, "E91", {"center": v(44.37, 130.93) * mm, "radius": 1.49 * mm});
            skLineSegment(sketch, "E92", {"start": v(-28.32, 98.9) * mm, "end": v(-28.32, 88.56) * mm, "construction": true});
            skLineSegment(sketch, "E93", {"start": v(44.37, 98.9) * mm, "end": v(44.37, 88.56) * mm});
            skPoint(sketch, "E93.startSnap0", {"position": v(44.37, 99.18) * mm});
            skLineSegment(sketch, "E94", {"start": v(-21.34, 98.9) * mm, "end": v(-21.34, 93.64) * mm, "construction": true});
            skSolve(sketch);
        }
        {
            var Q0;
            Q0 = qSketchRegion(id + "F10", true);
            extrude(context, id + "F11", {"entities" : qUnion([Q0]), "operationType" : NewBodyOperationType.REMOVE, "oppositeDirection" : true, "depth" : 25.4 * mm, "offsetDistance" : 25.4 * mm});
        }
        {
            var Q0;
            Q0=makeQuery(id+"F5.opExtrude","CAP_FACE",FACE,{"disambiguationData":[OSD([sQuery(id+"F4.wireOp",EDGE,"E36.bottom"),sQuery(id+"F4.wireOp",EDGE,"E36.top"),sQuery(id+"F4.wireOp",EDGE,"E36.left"),sQuery(id+"F4.wireOp",EDGE,"E36.right")])],"isStart":false});
            var sketch = newSketch(context, id + "F12", { "sketchPlane" : qUnion([Q0])});
            skLineSegment(sketch, "E95", {"start": v(-131.6, 73.32) * mm, "end": v(-43.21, -12.62) * mm});
            skLineSegment(sketch, "E96", {"start": v(-43.21, -12.62) * mm, "end": v(-43.21, -72.98) * mm});
            skLineSegment(sketch, "E97", {"start": v(-43.21, -72.98) * mm, "end": v(-145.1, -72.6) * mm});
            skLineSegment(sketch, "E98", {"start": v(-145.1, -72.6) * mm, "end": v(-131.46, 73.72) * mm});
            skSolve(sketch);
        }
        {
            var Q0;
            Q0 = qSketchRegion(id + "F12", true);
            extrude(context, id + "F13", {"entities" : qUnion([Q0]), "operationType" : NewBodyOperationType.REMOVE, "oppositeDirection" : true, "depth" : 25.4 * mm, "offsetDistance" : 25.4 * mm});
        }
        {
            var Q0;
            Q0=qCreatedBy(makeId("Right.planeOp"),FACE);
            cPlane(context, id + "F14", {"entities" : qUnion([Q0]), "cplaneType" : CPlaneType.OFFSET, "offset" : 25.4 * mm, "width" : 152.4 * mm, "height" : 152.4 * mm});
        }
        {
            var Q0;
            Q0=makeQuery(id+"F5.opExtrude","SWEPT_BODY",BODY,{"disambiguationData":[OSD([sQuery(id+"F4.wireOp",EDGE,"E36.bottom"),sQuery(id+"F4.wireOp",EDGE,"E36.top"),sQuery(id+"F4.wireOp",EDGE,"E36.left"),sQuery(id+"F4.wireOp",EDGE,"E36.right")])]});
            var Q1;
            Q1=qCreatedBy(id+"F14.planeOp",FACE);
            mirror(context, id + "F15", {"entities" : qUnion([Q0]), "mirrorPlane" : qUnion([Q1])});
        }
        {
            var Q0;
            Q0=makeQuery(id+"F15.opPattern","COPY",BODY,{"derivedFrom":makeQuery(id+"F5.opExtrude","SWEPT_BODY",BODY,{"disambiguationData":[OSD([sQuery(id+"F4.wireOp",EDGE,"E36.bottom"),sQuery(id+"F4.wireOp",EDGE,"E36.top"),sQuery(id+"F4.wireOp",EDGE,"E36.left"),sQuery(id+"F4.wireOp",EDGE,"E36.right")])]}),"instanceName":"1"});
            transform(context, id + "F16", {"entities" : qUnion([Q0]), "transformType" : TransformType.TRANSLATION_3D, "dx" : -226.57 * mm, "dy" : -115.06 * mm, "dz" : 0 * mm, "makeCopy" : false});
        }
        {
            var Q0;
            Q0=makeQuery(id+"F15.opPattern","COPY",BODY,{"derivedFrom":makeQuery(id+"F5.opExtrude","SWEPT_BODY",BODY,{"disambiguationData":[OSD([sQuery(id+"F4.wireOp",EDGE,"E36.bottom"),sQuery(id+"F4.wireOp",EDGE,"E36.top"),sQuery(id+"F4.wireOp",EDGE,"E36.left"),sQuery(id+"F4.wireOp",EDGE,"E36.right")])]}),"instanceName":"1"});
            var Q1;
            {var subQ0=sQuery(id+"F4.wireOp",EDGE,"E36.bottom");Q1=makeQuery(id+"F15.opPattern","COPY",EDGE,{"derivedFrom":makeQuery(id+"F7.boolean.opBoolean","SPLIT",EDGE,{"disambiguationData":[TD([makeQuery(id+"F7.opExtrude","SWEPT_FACE",FACE,{"disambiguationData":[OSD([sQuery(id+"F6.wireOp",EDGE,"E52.right")])]})])],"derivedFrom":makeQuery(id+"F5.opExtrude","CAP_EDGE",EDGE,{"disambiguationData":[OSD([subQ0])],"isStart":false})}),"instanceName":"1"});}
            transform(context, id + "F17", {"entities" : qUnion([Q0]), "transformType" : TransformType.ROTATION, "transformAxis" : qUnion([Q1]), "angle" : 180 * degree, "makeCopy" : false});
        }
        {
            var Q0;
            Q0=makeQuery(id+"F5.opExtrude","SWEPT_BODY",BODY,{"disambiguationData":[OSD([sQuery(id+"F4.wireOp",EDGE,"E36.bottom"),sQuery(id+"F4.wireOp",EDGE,"E36.top"),sQuery(id+"F4.wireOp",EDGE,"E36.left"),sQuery(id+"F4.wireOp",EDGE,"E36.right")])]});
            var Q1;
            Q1=makeQuery(id+"F15.opPattern","COPY",BODY,{"derivedFrom":makeQuery(id+"F5.opExtrude","SWEPT_BODY",BODY,{"disambiguationData":[OSD([sQuery(id+"F4.wireOp",EDGE,"E36.bottom"),sQuery(id+"F4.wireOp",EDGE,"E36.top"),sQuery(id+"F4.wireOp",EDGE,"E36.left"),sQuery(id+"F4.wireOp",EDGE,"E36.right")])]}),"instanceName":"1"});
            transform(context, id + "F18", {"entities" : qUnion([Q0, Q1]), "transformType" : TransformType.TRANSLATION_3D, "dx" : 7.11 * mm, "dy" : -35.56 * mm, "dz" : 0 * mm, "makeCopy" : false});
        }
        {
            var Q0;
            Q0=makeQuery(id+"F9.opExtrude","SWEPT_BODY",BODY,{"disambiguationData":[OSD([sQuery(id+"F8.wireOp",EDGE,"E63.bottom"),sQuery(id+"F8.wireOp",EDGE,"E63.top"),sQuery(id+"F8.wireOp",EDGE,"E63.left"),sQuery(id+"F8.wireOp",EDGE,"E63.right")])]});
            transform(context, id + "F19", {"entities" : qUnion([Q0]), "transformType" : TransformType.TRANSLATION_3D, "dx" : -87.38 * mm, "dy" : -36.07 * mm, "dz" : 0 * mm, "makeCopy" : false});
        }
        {
            var Q0;
            Q0=makeQuery(id+"F1.opExtrude","CAP_FACE",FACE,{"disambiguationData":[OSD([sQuery(id+"F0.wireOp",EDGE,"E0.bottom"),sQuery(id+"F0.wireOp",EDGE,"E0.top"),sQuery(id+"F0.wireOp",EDGE,"E0.left"),sQuery(id+"F0.wireOp",EDGE,"E0.right")])],"isStart":false});
            var sketch = newSketch(context, id + "F20", { "sketchPlane" : qUnion([Q0])});
            skArc(sketch, "E99", {"start": v(6.45, -40.06) * mm, "mid": v(3.55, -41.54) * mm, "end": v(3.28, -44.78) * mm});
            skArc(sketch, "E100", {"start": v(3.28, -44.78) * mm, "mid": v(5.88, -46.07) * mm, "end": v(8.48, -44.78) * mm});
            skArc(sketch, "E101", {"start": v(8.48, -44.78) * mm, "mid": v(7.45, -42.5) * mm, "end": v(4.97, -42.81) * mm});
            skArc(sketch, "E102", {"start": v(6.42, -40.72) * mm, "mid": v(3.76, -43.87) * mm, "end": v(7.78, -44.78) * mm});
            skArc(sketch, "E103", {"start": v(7.78, -44.78) * mm, "mid": v(6.95, -43.24) * mm, "end": v(5.23, -43.56) * mm});
            skLineSegment(sketch, "E104", {"start": v(6.45, -40.06) * mm, "end": v(6.42, -40.72) * mm});
            skLineSegment(sketch, "E105", {"start": v(4.97, -42.81) * mm, "end": v(5.23, -43.56) * mm});
            skSolve(sketch);
        }
        {
            var Q0;
            Q0 = qSketchRegion(id + "F20", true);
            extrude(context, id + "F21", {"entities" : qUnion([Q0]), "operationType" : NewBodyOperationType.REMOVE, "oppositeDirection" : true, "depth" : 25.4 * mm, "offsetDistance" : 25.4 * mm});
        }
        {
            var Q0;
            Q0=makeQuery(id+"F9.opExtrude","CAP_FACE",FACE,{"disambiguationData":[OSD([sQuery(id+"F8.wireOp",EDGE,"E63.bottom"),sQuery(id+"F8.wireOp",EDGE,"E63.top"),sQuery(id+"F8.wireOp",EDGE,"E63.left"),sQuery(id+"F8.wireOp",EDGE,"E63.right")])],"isStart":false});
            var sketch = newSketch(context, id + "F22", { "sketchPlane" : qUnion([Q0])});
            skArc(sketch, "E106", {"start": v(-79.5, 124.31) * mm, "mid": v(-82.4, 122.83) * mm, "end": v(-82.68, 119.59) * mm});
            skArc(sketch, "E107", {"start": v(-82.68, 119.59) * mm, "mid": v(-80.08, 118.3) * mm, "end": v(-77.48, 119.59) * mm});
            skArc(sketch, "E108", {"start": v(-77.48, 119.59) * mm, "mid": v(-78.5, 121.87) * mm, "end": v(-80.99, 121.56) * mm});
            skArc(sketch, "E109", {"start": v(-79.54, 123.65) * mm, "mid": v(-82.2, 120.5) * mm, "end": v(-78.18, 119.59) * mm});
            skArc(sketch, "E110", {"start": v(-78.18, 119.59) * mm, "mid": v(-79, 121.13) * mm, "end": v(-80.73, 120.81) * mm});
            skLineSegment(sketch, "E111", {"start": v(-79.5, 124.31) * mm, "end": v(-79.54, 123.65) * mm});
            skLineSegment(sketch, "E112", {"start": v(-80.99, 121.56) * mm, "end": v(-80.73, 120.81) * mm});
            skSolve(sketch);
        }
        {
            var Q0;
            Q0 = qSketchRegion(id + "F22", true);
            var Q1;
            Q1 = qConstructionFilter(qBodyType(qCreatedBy(id + "F22" ,EDGE), BodyType.WIRE), ConstructionObject.NO);
            extrude(context, id + "F23", {"entities" : qUnion([Q0]), "operationType" : NewBodyOperationType.REMOVE, "surfaceEntities" : qUnion([Q1]), "oppositeDirection" : true, "depth" : 25.4 * mm, "offsetDistance" : 25.4 * mm});
        }
        {
            var Q0;
            Q0=makeQuery(id+"F5.opExtrude","CAP_FACE",FACE,{"disambiguationData":[OSD([sQuery(id+"F4.wireOp",EDGE,"E36.bottom"),sQuery(id+"F4.wireOp",EDGE,"E36.top"),sQuery(id+"F4.wireOp",EDGE,"E36.left"),sQuery(id+"F4.wireOp",EDGE,"E36.right")])],"isStart":false});
            var sketch = newSketch(context, id + "F24", { "sketchPlane" : qUnion([Q0])});
            skArc(sketch, "E113", {"start": v(-68.48, 4.16) * mm, "mid": v(-71.6, 2.39) * mm, "end": v(-71.4, -1.2) * mm});
            skArc(sketch, "E114", {"start": v(-71.4, -1.2) * mm, "mid": v(-69.05, -2.1) * mm, "end": v(-66.7, -1.2) * mm});
            skArc(sketch, "E115", {"start": v(-66.7, -1.2) * mm, "mid": v(-67.23, 1.47) * mm, "end": v(-69.95, 1.35) * mm});
            skArc(sketch, "E116", {"start": v(-68.52, 3.4) * mm, "mid": v(-71.26, 0.83) * mm, "end": v(-68.1, -1.2) * mm});
            skArc(sketch, "E117", {"start": v(-68.1, -1.2) * mm, "mid": v(-68, 0.32) * mm, "end": v(-69.5, 0) * mm});
            skLineSegment(sketch, "E118", {"start": v(-68.48, 4.16) * mm, "end": v(-68.52, 3.4) * mm});
            skLineSegment(sketch, "E119", {"start": v(-69.95, 1.35) * mm, "end": v(-69.5, 0) * mm});
            skCircle(sketch, "E120", {"center": v(-57.9, 21.38) * mm, "radius": 1.59 * mm});
            skLineSegment(sketch, "E121", {"start": v(-57.9, 22.97) * mm, "end": v(-57.9, 28.84) * mm, "construction": true});
            skLineSegment(sketch, "E122", {"start": v(-57.9, 21.38) * mm, "end": v(-36.13, 21.38) * mm, "construction": true});
            skLineSegment(sketch, "E123", {"start": v(-57.9, 21.38) * mm, "end": v(-57.9, -26.98) * mm, "construction": true});
            skLineSegment(sketch, "E124", {"start": v(-57.9, 28.84) * mm, "end": v(-61.05, 28.84) * mm, "construction": true});
            skLineSegment(sketch, "E125", {"start": v(-57.9, 28.84) * mm, "end": v(-54.75, 28.84) * mm, "construction": true});
            skCircle(sketch, "E126", {"center": v(-53.2, 28.84) * mm, "radius": 1.56 * mm});
            skCircle(sketch, "E127", {"center": v(-62.61, 28.84) * mm, "radius": 1.56 * mm});
            skSolve(sketch);
        }
        {
            var Q0;
            Q0 = qSketchRegion(id + "F24", true);
            extrude(context, id + "F25", {"entities" : qUnion([Q0]), "operationType" : NewBodyOperationType.REMOVE, "oppositeDirection" : true, "depth" : 25.4 * mm, "offsetDistance" : 25.4 * mm});
        }
        {
            var Q0;
            Q0=makeQuery(id+"F15.opPattern","COPY",FACE,{"derivedFrom":makeQuery(id+"F5.opExtrude","CAP_FACE",FACE,{"disambiguationData":[OSD([sQuery(id+"F4.wireOp",EDGE,"E36.bottom"),sQuery(id+"F4.wireOp",EDGE,"E36.top"),sQuery(id+"F4.wireOp",EDGE,"E36.left"),sQuery(id+"F4.wireOp",EDGE,"E36.right")])],"isStart":true}),"instanceName":"1"});
            var sketch = newSketch(context, id + "F26", { "sketchPlane" : qUnion([Q0])});
            skArc(sketch, "E128", {"start": v(-87.7, -20.93) * mm, "mid": v(-90.74, -22.48) * mm, "end": v(-91.02, -25.86) * mm});
            skArc(sketch, "E129", {"start": v(-91.02, -25.86) * mm, "mid": v(-88.3, -27.2) * mm, "end": v(-85.6, -25.86) * mm});
            skArc(sketch, "E130", {"start": v(-85.6, -25.86) * mm, "mid": v(-86.67, -23.48) * mm, "end": v(-89.26, -23.8) * mm});
            skArc(sketch, "E131", {"start": v(-87.74, -21.62) * mm, "mid": v(-90.52, -24.91) * mm, "end": v(-86.32, -25.86) * mm});
            skArc(sketch, "E132", {"start": v(-86.32, -25.86) * mm, "mid": v(-87.19, -24.25) * mm, "end": v(-88.99, -24.58) * mm});
            skLineSegment(sketch, "E133", {"start": v(-87.7, -20.93) * mm, "end": v(-87.74, -21.62) * mm});
            skLineSegment(sketch, "E134", {"start": v(-89.26, -23.8) * mm, "end": v(-88.99, -24.58) * mm});
            skLineSegment(sketch, "E135", {"start": v(-103.64, -60.66) * mm, "end": v(-103.64, -35.26) * mm, "construction": true});
            skCircle(sketch, "E136", {"center": v(-103.64, -35.26) * mm, "radius": 1.59 * mm});
            skLineSegment(sketch, "E137", {"start": v(-103.64, -36.85) * mm, "end": v(-103.64, -42.71) * mm, "construction": true});
            skLineSegment(sketch, "E138", {"start": v(-103.64, -42.71) * mm, "end": v(-100.5, -42.71) * mm, "construction": true});
            skLineSegment(sketch, "E139", {"start": v(-103.64, -42.71) * mm, "end": v(-106.8, -42.71) * mm, "construction": true});
            skCircle(sketch, "E140", {"center": v(-108.35, -42.71) * mm, "radius": 1.56 * mm});
            skCircle(sketch, "E141", {"center": v(-98.93, -42.71) * mm, "radius": 1.56 * mm});
            skSolve(sketch);
        }
        {
            var Q0;
            Q0 = qSketchRegion(id + "F26", true);
            extrude(context, id + "F27", {"entities" : qUnion([Q0]), "operationType" : NewBodyOperationType.REMOVE, "oppositeDirection" : true, "depth" : 25.4 * mm, "offsetDistance" : 25.4 * mm});
        }
        {
            var Q0;
            Q0=makeQuery(id+"F5.opExtrude","SWEPT_BODY",BODY,{"disambiguationData":[OSD([sQuery(id+"F4.wireOp",EDGE,"E36.bottom"),sQuery(id+"F4.wireOp",EDGE,"E36.top"),sQuery(id+"F4.wireOp",EDGE,"E36.left"),sQuery(id+"F4.wireOp",EDGE,"E36.right")])]});
            var Q1;
            Q1=makeQuery(id+"F9.opExtrude","SWEPT_BODY",BODY,{"disambiguationData":[OSD([sQuery(id+"F8.wireOp",EDGE,"E63.bottom"),sQuery(id+"F8.wireOp",EDGE,"E63.top"),sQuery(id+"F8.wireOp",EDGE,"E63.left"),sQuery(id+"F8.wireOp",EDGE,"E63.right")])]});
            transform(context, id + "F28", {"entities" : qUnion([Q0, Q1]), "transformType" : TransformType.TRANSLATION_3D, "dx" : -50.8 * mm, "dy" : 0 * mm, "dz" : 0 * mm, "makeCopy" : false});
        }
        {
            var Q0;
            Q0=makeQuery(id+"F9.opExtrude","SWEPT_BODY",BODY,{"disambiguationData":[OSD([sQuery(id+"F8.wireOp",EDGE,"E63.bottom"),sQuery(id+"F8.wireOp",EDGE,"E63.top"),sQuery(id+"F8.wireOp",EDGE,"E63.left"),sQuery(id+"F8.wireOp",EDGE,"E63.right")])]});
            transform(context, id + "F29", {"entities" : qUnion([Q0]), "transformType" : TransformType.TRANSLATION_3D, "dx" : 38.1 * mm, "dy" : 50.8 * mm, "dz" : 0 * mm, "makeCopy" : false});
        }
    });
